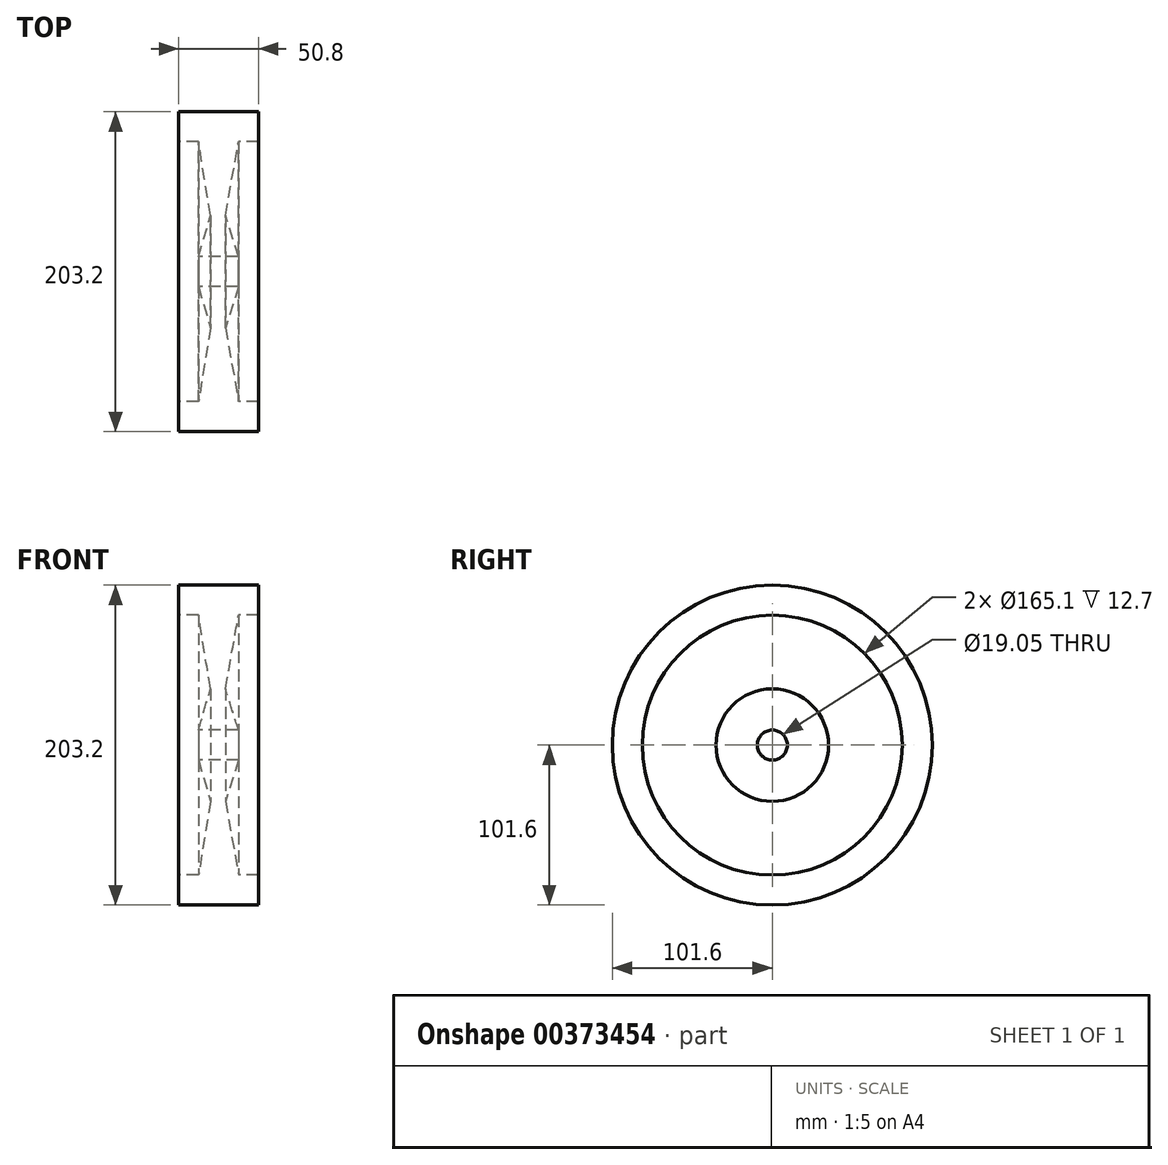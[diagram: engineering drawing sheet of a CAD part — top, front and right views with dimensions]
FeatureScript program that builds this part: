
annotation { "Feature Type Name" : "Feature", "Feature Type Description" : "" }
export const myFeature = defineFeature(function(context is Context, id is Id, definition is map)
    precondition{}
    {
        {
            var Q0;
            Q0=qCreatedBy(makeId("Front.planeOp"),FACE);
            var sketch = newSketch(context, id + "F0", { "sketchPlane" : qUnion([Q0])});
            skLineSegment(sketch, "E0", {"start": v(-22.38, 0) * mm, "end": v(34.33, 0) * mm});
            skLineSegment(sketch, "E1", {"start": v(-12.7, 9.52) * mm, "end": v(12.7, 9.53) * mm});
            skLineSegment(sketch, "E2", {"start": v(12.7, 9.53) * mm, "end": v(4.35, 35.76) * mm});
            skLineSegment(sketch, "E3", {"start": v(4.35, 35.76) * mm, "end": v(12.7, 82.55) * mm});
            skLineSegment(sketch, "E4", {"start": v(12.7, 82.55) * mm, "end": v(25.4, 82.55) * mm});
            skLineSegment(sketch, "E5", {"start": v(25.4, 82.55) * mm, "end": v(25.4, 101.6) * mm});
            skLineSegment(sketch, "E6", {"start": v(25.4, 101.6) * mm, "end": v(-25.4, 101.6) * mm});
            skLineSegment(sketch, "E7", {"start": v(-25.4, 101.6) * mm, "end": v(-25.4, 82.55) * mm});
            skLineSegment(sketch, "E8", {"start": v(-25.4, 82.55) * mm, "end": v(-12.7, 82.55) * mm});
            skLineSegment(sketch, "E9", {"start": v(-12.7, 82.55) * mm, "end": v(-5.14, 35.76) * mm});
            skLineSegment(sketch, "E10", {"start": v(-5.14, 35.76) * mm, "end": v(-12.7, 9.52) * mm});
            skSolve(sketch);
        }
        {
            var Q0;
            Q0=makeQuery(id+"F0.imprint","IMPRINT",FACE,{"disambiguationData":[TD([[makeQuery(id+"F0.imprint","IMPRINT",EDGE,{"derivedFrom":sQuery(id+"F0.wireOp",EDGE,"E1")}),1.0]])]});
            var Q1;
            Q1=sQuery(id+"F0.wireOp",EDGE,"E0");
            revolve(context, id + "F1", {"entities" : qUnion([Q0]), "axis" : qUnion([Q1]), "revolveType" : RevolveType.FULL});
        }
    });
